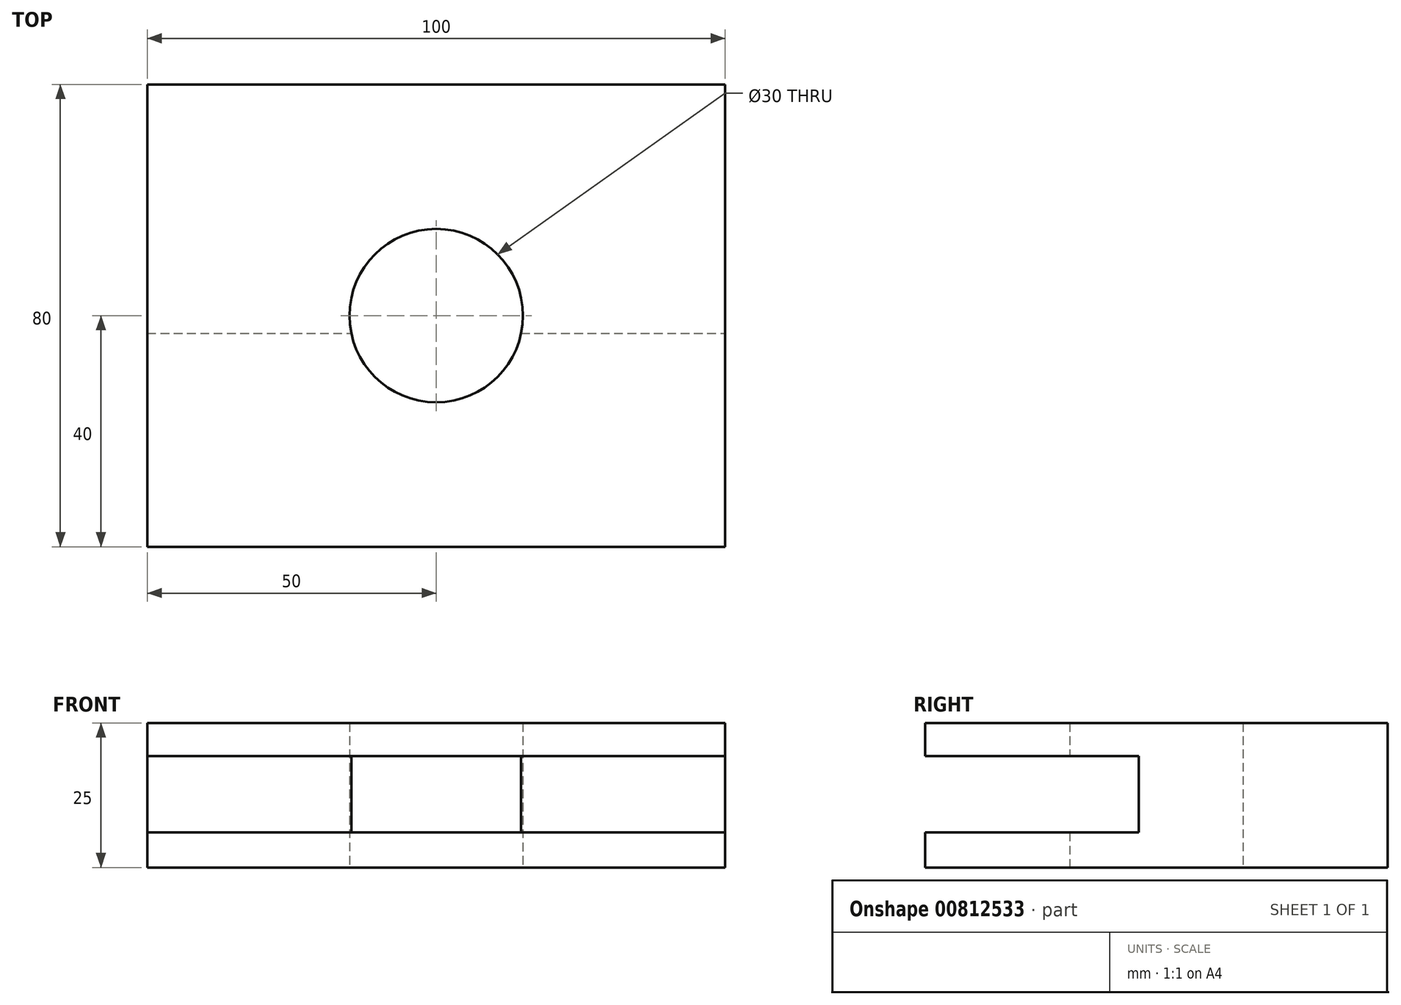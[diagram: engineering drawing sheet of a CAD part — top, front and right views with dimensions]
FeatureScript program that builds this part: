
annotation { "Feature Type Name" : "Feature", "Feature Type Description" : "" }
export const myFeature = defineFeature(function(context is Context, id is Id, definition is map)
    precondition{}
    {
        {
            var Q0;
            Q0=qCreatedBy(makeId("Top.planeOp"),FACE);
            var sketch = newSketch(context, id + "F0", { "sketchPlane" : qUnion([Q0])});
            skLineSegment(sketch, "E0.bottom", {"start": v(-50, 40) * mm, "end": v(50, 40) * mm});
            skLineSegment(sketch, "E0.top", {"start": v(-50, -40) * mm, "end": v(50, -40) * mm});
            skLineSegment(sketch, "E0.left", {"start": v(-50, 40) * mm, "end": v(-50, -40) * mm});
            skLineSegment(sketch, "E0.right", {"start": v(50, 40) * mm, "end": v(50, -40) * mm});
            skCircle(sketch, "E1", {"center": v(0, 0) * mm, "radius": 15 * mm});
            skSolve(sketch);
        }
        {
            var Q0;
            Q0=makeQuery(id+"F0.imprint","IMPRINT",FACE,{"disambiguationData":[TD([[makeQuery(id+"F0.imprint","IMPRINT",EDGE,{"derivedFrom":sQuery(id+"F0.wireOp",EDGE,"E0.bottom")}),-1.0]])]});
            extrude(context, id + "F1", {"entities" : qUnion([Q0]), "depth" : 25 * mm, "offsetDistance" : 25 * mm});
        }
        {
            var Q0;
            Q0=qCreatedBy(makeId("Right.planeOp"),FACE);
            var sketch = newSketch(context, id + "F2", { "sketchPlane" : qUnion([Q0])});
            skLineSegment(sketch, "E2.bottom", {"start": v(-50.46, 19.28) * mm, "end": v(-3.07, 19.28) * mm});
            skLineSegment(sketch, "E2.top", {"start": v(-50.46, 6.04) * mm, "end": v(-3.07, 6.04) * mm});
            skLineSegment(sketch, "E2.left", {"start": v(-50.46, 19.28) * mm, "end": v(-50.46, 6.04) * mm});
            skLineSegment(sketch, "E2.right", {"start": v(-3.07, 19.28) * mm, "end": v(-3.07, 6.04) * mm});
            skSolve(sketch);
        }
        {
            var Q0;
            Q0=makeQuery(id+"F2.imprint","IMPRINT",FACE,{"disambiguationData":[TD([[makeQuery(id+"F2.imprint","IMPRINT",EDGE,{"derivedFrom":sQuery(id+"F2.wireOp",EDGE,"E2.bottom")}),-1.0]])]});
            extrude(context, id + "F3", {"entities" : qUnion([Q0]), "operationType" : NewBodyOperationType.REMOVE, "endBound" : BoundingType.SYMMETRIC, "oppositeDirection" : true, "depth" : 100 * mm, "offsetDistance" : 25 * mm});
        }
    });
